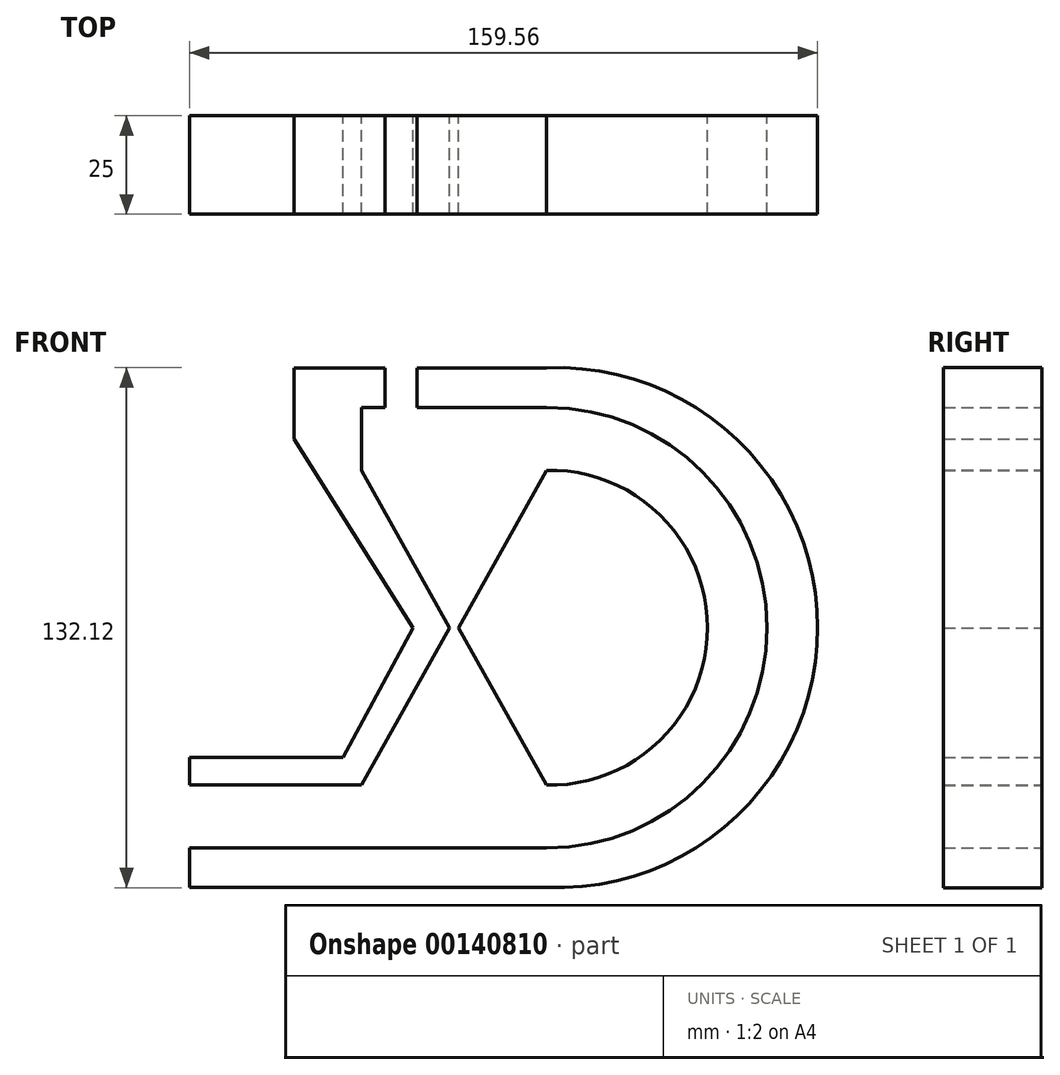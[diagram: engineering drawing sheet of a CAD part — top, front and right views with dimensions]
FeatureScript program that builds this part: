
annotation { "Feature Type Name" : "Feature", "Feature Type Description" : "" }
export const myFeature = defineFeature(function(context is Context, id is Id, definition is map)
    precondition{}
    {
        {
            var Q0;
            Q0=qCreatedBy(makeId("Front.planeOp"),FACE);
            var sketch = newSketch(context, id + "F0", { "sketchPlane" : qUnion([Q0])});
            skLineSegment(sketch, "E0", {"start": v(23.49, 56) * mm, "end": v(23.49, 0) * mm, "construction": true});
            skLineSegment(sketch, "E1.MirrorCS", {"start": v(23.49, -56) * mm, "end": v(23.49, 0) * mm, "construction": true});
            skArc(sketch, "E2", {"start": v(23.49, -56) * mm, "mid": v(79.49, 0) * mm, "end": v(23.49, 56) * mm});
            skLineSegment(sketch, "E3", {"start": v(23.49, 0) * mm, "end": v(23.49, 40) * mm, "construction": true});
            skLineSegment(sketch, "E4.MirrorCS", {"start": v(23.49, 0) * mm, "end": v(23.49, -40) * mm, "construction": true});
            skLineSegment(sketch, "E5.MirrorCS", {"start": v(-1.17, 0) * mm, "end": v(-23.49, 40) * mm});
            skLineSegment(sketch, "E6.MirrorCS", {"start": v(-1.17, 0) * mm, "end": v(-23.49, -40) * mm});
            skLineSegment(sketch, "E7.MirrorCS", {"start": v(-67.22, -56) * mm, "end": v(23.49, -56) * mm});
            skLineSegment(sketch, "E8", {"start": v(-23.49, -40) * mm, "end": v(-67.18, -40) * mm});
            skLineSegment(sketch, "E9", {"start": v(-23.49, 40) * mm, "end": v(-23.49, 56) * mm});
            skLineSegment(sketch, "E10.MirrorCS", {"start": v(1.17, 0) * mm, "end": v(23.49, 40) * mm});
            skLineSegment(sketch, "E11.MirrorCS", {"start": v(1.17, 0) * mm, "end": v(23.49, -40) * mm});
            skArc(sketch, "E12", {"start": v(23.49, -40) * mm, "mid": v(64.38, 0) * mm, "end": v(23.49, 40) * mm});
            skLineSegment(sketch, "E13", {"start": v(23.49, 0) * mm, "end": v(23.49, 66) * mm, "construction": true});
            skLineSegment(sketch, "E14.MirrorCS", {"start": v(23.49, 0) * mm, "end": v(23.49, -66) * mm, "construction": true});
            skArc(sketch, "E15", {"start": v(23.49, -66) * mm, "mid": v(92.34, 0) * mm, "end": v(23.49, 66) * mm});
            skLineSegment(sketch, "E16", {"start": v(23.49, -66) * mm, "end": v(-67.22, -66) * mm});
            skLineSegment(sketch, "E17", {"start": v(-67.22, -66) * mm, "end": v(-67.22, -56) * mm});
            skLineSegment(sketch, "E18", {"start": v(-40.62, 66) * mm, "end": v(-40.62, 47.92) * mm});
            skLineSegment(sketch, "E19", {"start": v(-40.62, 47.92) * mm, "end": v(-10.4, 0) * mm});
            skLineSegment(sketch, "E20", {"start": v(-67.18, -40) * mm, "end": v(-67.18, -32.97) * mm});
            skLineSegment(sketch, "E21", {"start": v(-67.18, -32.97) * mm, "end": v(-28.26, -32.97) * mm});
            skLineSegment(sketch, "E22", {"start": v(-28.26, -32.97) * mm, "end": v(-10.4, 0) * mm});
            skLineSegment(sketch, "E23", {"start": v(-40.62, 66) * mm, "end": v(-17.6, 66) * mm});
            skLineSegment(sketch, "E24", {"start": v(-23.49, 56) * mm, "end": v(-17.6, 56) * mm});
            skLineSegment(sketch, "E25", {"start": v(-17.6, 56) * mm, "end": v(-17.6, 66) * mm});
            skLineSegment(sketch, "E26", {"start": v(-9.44, 66) * mm, "end": v(23.49, 66) * mm});
            skLineSegment(sketch, "E27", {"start": v(23.49, 56) * mm, "end": v(-9.44, 56) * mm});
            skLineSegment(sketch, "E28", {"start": v(-9.44, 66) * mm, "end": v(-9.44, 56) * mm});
            skSolve(sketch);
        }
        {
            var Q0;
            Q0=makeQuery(id+"F0.imprint","IMPRINT",FACE,{"disambiguationData":[TD([[makeQuery(id+"F0.imprint","IMPRINT",EDGE,{"derivedFrom":sQuery(id+"F0.wireOp",EDGE,"E2")}),-1.0]])]});
            var Q1;
            Q1=makeQuery(id+"F0.imprint","IMPRINT",FACE,{"disambiguationData":[TD([[makeQuery(id+"F0.imprint","IMPRINT",EDGE,{"derivedFrom":sQuery(id+"F0.wireOp",EDGE,"E10.MirrorCS")}),-1.0]])]});
            var Q2;
            Q2=makeQuery(id+"F0.imprint","IMPRINT",FACE,{"disambiguationData":[TD([[makeQuery(id+"F0.imprint","IMPRINT",EDGE,{"derivedFrom":sQuery(id+"F0.wireOp",EDGE,"E5.MirrorCS")}),1.0]])]});
            extrude(context, id + "F1", {"entities" : qUnion([Q0, Q1, Q2]), "depth" : 25 * mm});
        }
    });
